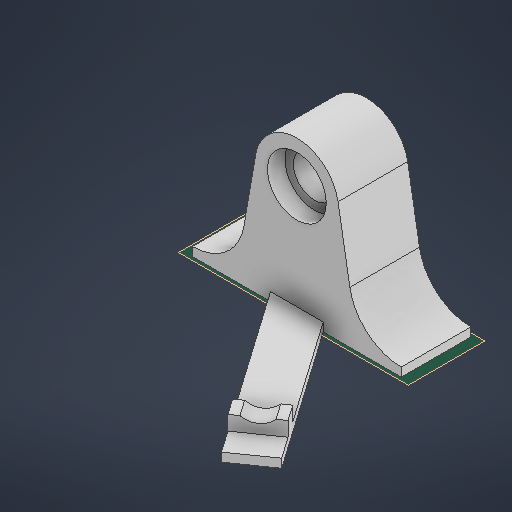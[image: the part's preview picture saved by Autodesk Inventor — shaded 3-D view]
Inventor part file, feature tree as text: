
AUTODESK INVENTOR PART (.ipt)
format: ipt  version: 2025.3 (Build 293356030, 356C)  size: 272,384 bytes
history: native  units: mm
features: extrude x7, sketch x3, plane x1, projected_geometry x1
ambient origin geometry x8: Origin, YZ Plane, XZ Plane, XY Plane, X Axis, Y Axis, Z Axis, Center Point
bodies: Solid1 (feature_tree)
feature tree (12):
  sketch  "Sketch1"  dims[d0=16.9mm d1=12.0mm d2=30.0mm d3=12.0mm d4=15.0mm d5=60.0mm d6=2.5mm d7=20.0mm d8=0.0mm]
  extrude  "Extrusion1"  Depth=20.0mm TaperAngle=0.0deg
  extrude  "Extrusion2"  Depth=20.0mm TaperAngle=0.0deg
  extrude  "Extrusion3"  Depth=7.5mm
  plane  "Work Plane1"
  sketch  "Sketch2"  dims[d9=15.0mm d10=0.0mm d11=20.0mm d12=0.0mm]
  extrude  "Extrusion6"  Depth=5.5mm
  sketch  "Sketch4"  dims[d13=0.0mm d14=6.108652mm d16=5.5mm d17=20.0mm d26=40.0mm d27=2.5mm d28=0.0mm d29=14.6mm d30=10.7mm d31=1.5mm d32=8.0mm d33=5.5mm d34=0.0mm d35=5.5mm d36=0.0mm d37=7.5mm d38=0.0mm]
  extrude  "Extrusion7"  Depth=20.0mm
  extrude  "Extrusion8"  Depth=7.5mm
  extrude  "Extrusion9"  Depth=2.5mm TaperAngle=0.0deg
  projected_geometry  "Projected Loop2"
